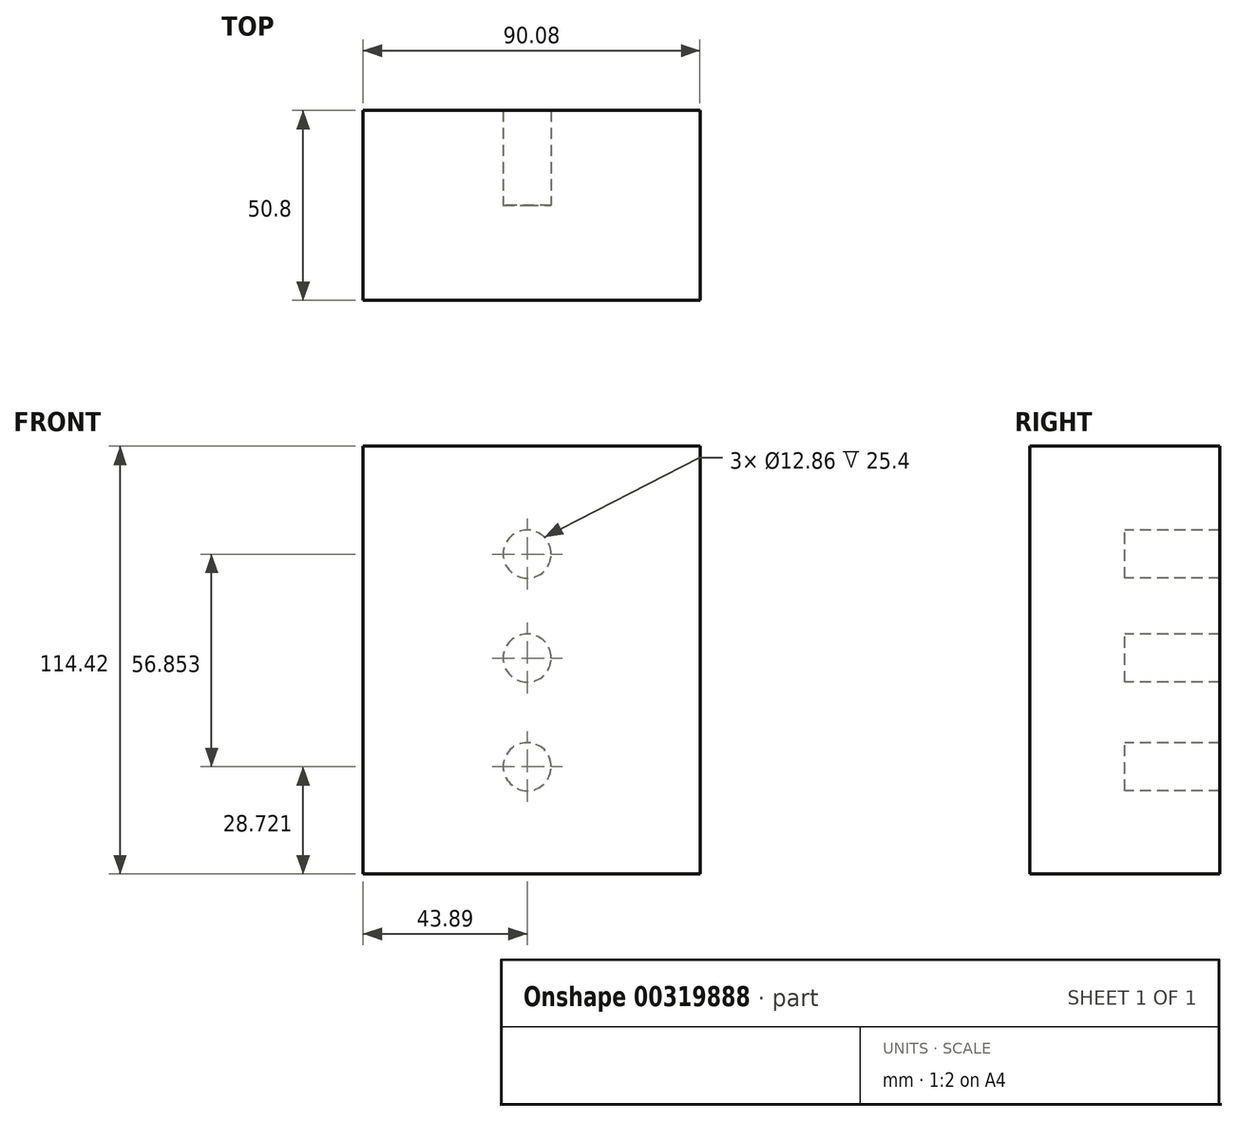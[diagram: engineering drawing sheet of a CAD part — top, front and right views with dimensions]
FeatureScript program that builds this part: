
annotation { "Feature Type Name" : "Feature", "Feature Type Description" : "" }
export const myFeature = defineFeature(function(context is Context, id is Id, definition is map)
    precondition{}
    {
        {
            var Q0;
            Q0=qCreatedBy(makeId("Front.planeOp"),FACE);
            var sketch = newSketch(context, id + "F0", { "sketchPlane" : qUnion([Q0])});
            skLineSegment(sketch, "E0.bottom", {"start": v(-43.89, 56.66) * mm, "end": v(46.2, 56.66) * mm});
            skLineSegment(sketch, "E0.top", {"start": v(-43.89, -57.76) * mm, "end": v(46.2, -57.76) * mm});
            skLineSegment(sketch, "E0.left", {"start": v(-43.89, 56.66) * mm, "end": v(-43.89, -57.76) * mm});
            skLineSegment(sketch, "E0.right", {"start": v(46.2, 56.66) * mm, "end": v(46.2, -57.76) * mm});
            skSolve(sketch);
        }
        {
            var Q0;
            Q0 = qSketchRegion(id + "F0", true);
            extrude(context, id + "F1", {"entities" : qUnion([Q0]), "depth" : 50.8 * mm});
        }
        {
            var Q0;
            Q0=qCreatedBy(makeId("Front.planeOp"),FACE);
            var sketch = newSketch(context, id + "F2", { "sketchPlane" : qUnion([Q0])});
            skCircle(sketch, "E1", {"center": v(0, 27.81) * mm, "radius": 6.43 * mm});
            skCircle(sketch, "E2", {"center": v(0, 0) * mm, "radius": 6.43 * mm});
            skCircle(sketch, "E3", {"center": v(0, -29.04) * mm, "radius": 6.43 * mm});
            skSolve(sketch);
        }
        {
            var Q0;
            Q0 = qSketchRegion(id + "F2", true);
            extrude(context, id + "F3", {"entities" : qUnion([Q0]), "operationType" : NewBodyOperationType.REMOVE, "oppositeDirection" : true, "depth" : 50.8 * mm, "hasSecondDirection" : true, "secondDirectionOppositeDirection" : false, "secondDirectionDepth" : 25.4 * mm});
        }
    });
